# Revit family: Agta_Record_RlvngDrsetSym_K21
name_source: partatom
category: Doors
revit_build: Autodesk Revit Architecture 2012 (Build: 20110916_2132(x64)
units: mm (PartAtom-declared; Revit-internal decimal feet)

## types (1)
- Default
    AccessoryOptions = Contact manufacturer
    AlternativeDoorsetGlazing = Part of glazing spec
    AntiFingerTrapRequirement = Yes
    Assembly Code = B2030300
    BIMObjectName = K21.rfa
    BottomConstruction = Revolving Door, Stainless Steel
    CanopyCovering = Revolving Door, Sheet metal (Painted Steel)
    CanopyHeight = 570.00 mm
    CanopyHeightOptions = 350 mm +
    CanopyRadius = 2479.00 mm
    Capacity = <>
    Colour = Customer specific
    Configuration = 2, 3 or 4 leafs
    Construction Type = Automatic Revolving Door
    Cost = 0 $
    DepthOfRecessFloorFrame = 80.00 mm
    Description = 2-wing Revolving Door
    DiameterOptions = Internal: 3400 - 6500 mm
    DoorOpening = 0.00 mm
    DoorSeal = 1
    DoorWingOptions = 2 wings
    DoorsetFasteners = Screws
    DoorsetOperation = Automatic
    DoorsetOptions = Ridig, Sliding door, Display case
    DrumWallPanelFill = Revolving Door, Laminated Safety Glass (Clear)
    ElectronicLock = Yes
    ExternalDimensionOfFloorFrame = 5056.00 mm
    Finish = Powder coated, Anodized, customer specific
    FireExit = No
    FloorFrame(Ring) = Yes
    Flooring = Revolving Door, Felt Carpet
    FrameMaterial = Aluminium
    FrameProfile = Aluminium
    FrameSeal = Yes
    Function = Exterior
    GlassLayers = 1
    GlassThickness1 = 0.00 mm
    GlassThickness2 = 0.00 mm
    GlassType = Part of glazing spec
    HandicapAccessible = No
    HasDrive = Yes
    Height = 2595.00 mm
    HeightOfFloorFrame = 65.00 mm
    HeightUnderCanopyOptions = Passage height: 2000 - 3000 mm
    IfcExportAs = IfcDoorStyle
    IfcExportType = Door
    InnerRadius = 2400.00 mm
    InsideDiameter = 4800.00 mm
    IsExternal = Yes
    LeafColourOptions = All RAL, customer specific
    LeafPanelFill = Revolving Door, Laminated Safety Glass (Clear)
    Manufacturer = Record
    ManufacturerName = Record
    ManufacturerURL = www.agta-record.com
    Material = Aluminium
    Model = K21
    ModelReference = Depends on the configuration
    NBSDescription = 2-wing Revolving Door
    NBSReference = 25-50-20/170
    NominalHeight = 2570.00 mm
    NominalLength = 4958.00 mm
    NominalWidth = 4958.00 mm
    OpenSlidingDoor(Center) = No
    OpeningRotationAngle = 90.00°
    OperatingTemperature = -15° to +50°C
    OuterRadius = 2426.00 mm
    OutsideDiameter = 4852.00 mm
    PanelFrames = Revolving Door, Aluminium
    PassageHeight = 2000.00 mm
    PassageWidth = 2692.00 mm
    PassageWidthInsideDoor = 2240.00 mm
    ProductInformation = www.agta-record.com
    RecessHeight = 2620.00 mm
    RecessWidth = 5058.00 mm
    ReferenceStandard = EN16005, EN16361, DIN 18650, etc.
    ReplacementCost = Depends on the configuration and door type
    RevolvingRadius = 2344.00 mm
    Rough Height = 2576.00 mm
    Rough Width = 4964.00 mm
    SafetyDevices = Fully compliant with EN16005, Safety buffers, Presence sensors, etc.
    SelfClosing = Yes
    ServiceLifeDuration = 10-15 years
    Shape = Cylinder shaped
    ShowcaseRadius = 2324.00 mm
    ShowcaseVisibility = Yes
    SmokeStop = No
    SpotLightRadius = 1921.00 mm
    ThermalTransmittance = 0
    ThresholdRequired = Yes
    ThresholdStripping = No additional required, part of the doorset
    TotalDiameter = 4958.00 mm
    TotalHeight = 2570.00 mm
    URL = www.agta-record.com
    Uniclass2 = Ss_25_30_20_70
    Version = Version 1.0
    WarrantyDescription = Depends on country
    WarrantyDurationLabour = Depends on country
    WarrantyDurationParts = Depends on country
    WarrantyDurationUnit = Depends on country
    WarrantyGuarantorLabour = Local door manufacturer
    WarrantyGuarantorParts = Local door manufacturer
    WarrantyStartDate = Depends on country
    Weight = Depends on configuration and size
    Width = 4877.00 mm
    WithinStandardSizes = Yes

## geometry (parser evidence)
native form markers: Blend x12, Sweep x14
no freeform markers — native parametric forms only
